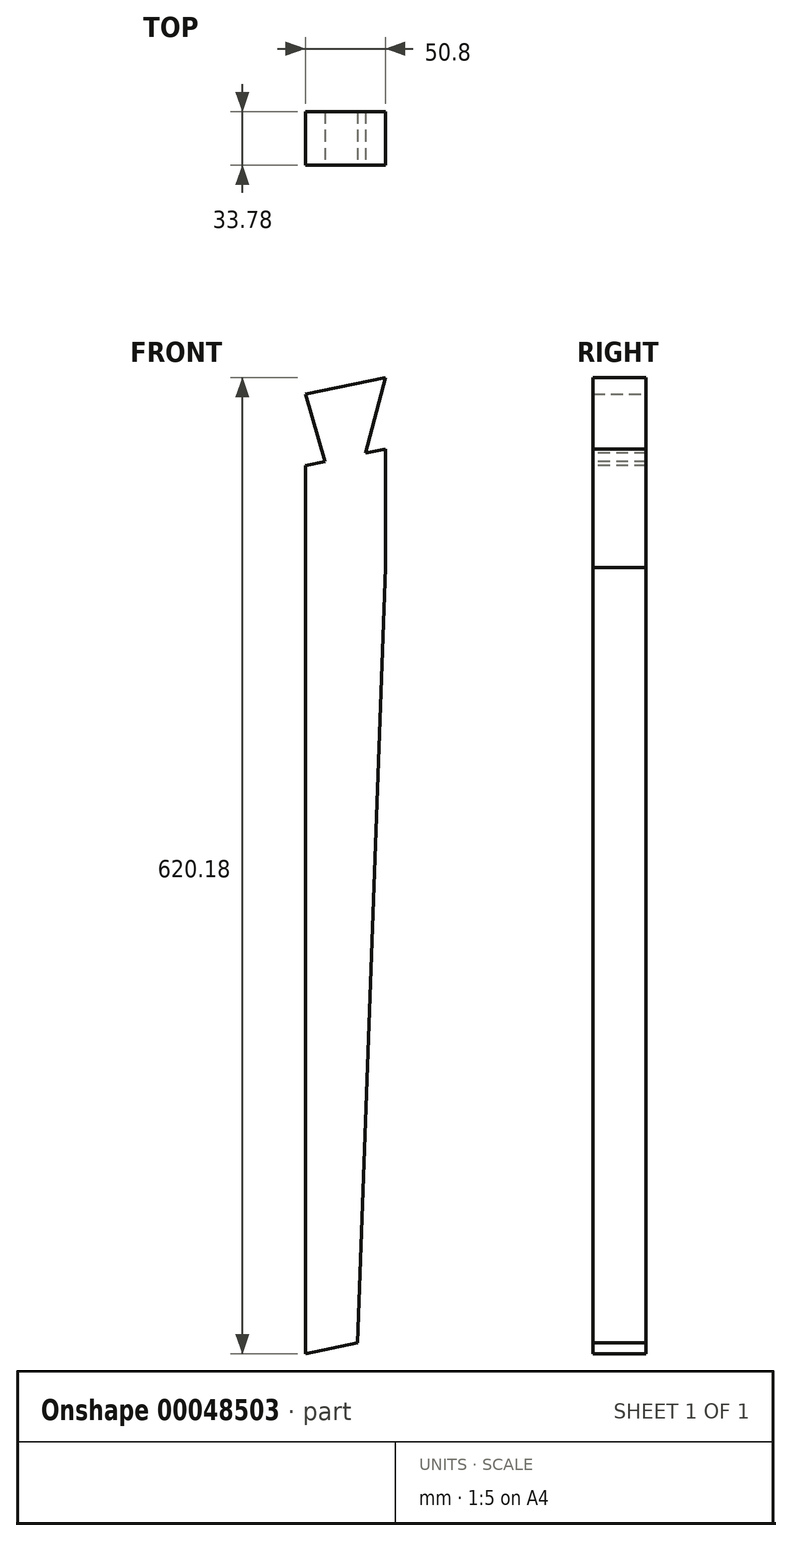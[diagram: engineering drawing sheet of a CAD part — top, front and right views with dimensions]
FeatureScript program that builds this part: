
annotation { "Feature Type Name" : "Feature", "Feature Type Description" : "" }
export const myFeature = defineFeature(function(context is Context, id is Id, definition is map)
    precondition{}
    {
        {
            var Q0;
            Q0=qCreatedBy(makeId("Front.planeOp"),FACE);
            var sketch = newSketch(context, id + "F0", { "sketchPlane" : qUnion([Q0])});
            skLineSegment(sketch, "E0.bottom", {"start": v(-25.4, 304.8) * mm, "end": v(25.4, 304.8) * mm});
            skLineSegment(sketch, "E0.top", {"start": v(-25.4, -315.38) * mm, "end": v(25.4, -315.38) * mm});
            skLineSegment(sketch, "E0.left", {"start": v(-25.4, 304.8) * mm, "end": v(-25.4, -315.38) * mm});
            skLineSegment(sketch, "E0.right", {"start": v(25.4, 304.8) * mm, "end": v(25.4, -315.38) * mm});
            skLineSegment(sketch, "E1", {"start": v(25.4, 304.8) * mm, "end": v(-584.2, 304.8) * mm, "construction": true});
            skLineSegment(sketch, "E2", {"start": v(-584.2, 304.8) * mm, "end": v(-584.2, 177.8) * mm, "construction": true});
            skLineSegment(sketch, "E3", {"start": v(-584.2, 177.8) * mm, "end": v(25.4, 304.8) * mm, "construction": true});
            skLineSegment(sketch, "E4", {"start": v(25.4, 304.8) * mm, "end": v(-25.4, 294.22) * mm});
            skLineSegment(sketch, "E5", {"start": v(-25.4, -315.38) * mm, "end": v(584.2, -315.38) * mm, "construction": true});
            skLineSegment(sketch, "E6", {"start": v(584.2, -315.38) * mm, "end": v(584.2, -188.38) * mm, "construction": true});
            skLineSegment(sketch, "E7", {"start": v(584.2, -188.38) * mm, "end": v(-25.4, -315.38) * mm, "construction": true});
            skLineSegment(sketch, "E8", {"start": v(-25.4, -315.38) * mm, "end": v(25.4, -304.8) * mm});
            skSolve(sketch);
        }
        {
            var Q0;
            {var subQ2=sQuery(id+"F0.wireOp",EDGE,"E4");Q0=makeQuery(id+"F0.imprint","IMPRINT",FACE,{"disambiguationData":[TD([[makeQuery(id+"F0.imprint","IMPRINT",EDGE,{"derivedFrom":subQ2}),1.0]])]});}
            extrude(context, id + "F1", {"entities" : qUnion([Q0]), "depth" : 33.78 * mm});
        }
        {
            var Q0;
            Q0=makeQuery(id+"F1.opExtrude","CAP_FACE",FACE,{"disambiguationData":[OSD([sQuery(id+"F0.wireOp",EDGE,"E0.left"),sQuery(id+"F0.wireOp",EDGE,"E0.right"),sQuery(id+"F0.wireOp",EDGE,"E4"),sQuery(id+"F0.wireOp",EDGE,"E8")])],"isStart":false});
            var sketch = newSketch(context, id + "F2", { "sketchPlane" : qUnion([Q0])});
            skLineSegment(sketch, "E9", {"start": v(-25.4, -315.38) * mm, "end": v(7.67, -308.5) * mm});
            skLineSegment(sketch, "E10", {"start": v(7.67, -308.5) * mm, "end": v(25.4, 184.15) * mm});
            skSolve(sketch);
        }
        {
            var Q0;
            {var subQ0=sQuery(id+"F2.wireOp",EDGE,"E10");Q0=makeQuery(id+"F2.imprint","IMPRINT",FACE,{"disambiguationData":[TD([[makeQuery(id+"F2.imprint","IMPRINT",EDGE,{"derivedFrom":subQ0}),-1.0]])]});}
            extrude(context, id + "F3", {"entities" : qUnion([Q0]), "operationType" : NewBodyOperationType.REMOVE, "endBound" : BoundingType.THROUGH_ALL, "oppositeDirection" : true, "depth" : 25.4 * mm});
        }
        {
            var Q0;
            Q0=makeQuery(id+"F1.opExtrude","CAP_FACE",FACE,{"disambiguationData":[OSD([sQuery(id+"F0.wireOp",EDGE,"E0.left"),sQuery(id+"F0.wireOp",EDGE,"E0.right"),sQuery(id+"F0.wireOp",EDGE,"E4"),sQuery(id+"F0.wireOp",EDGE,"E8")])],"isStart":false});
            var sketch = newSketch(context, id + "F4", { "sketchPlane" : qUnion([Q0])});
            skLineSegment(sketch, "E11", {"start": v(-25.4, 248.81) * mm, "end": v(25.4, 259.4) * mm, "construction": true});
            skLineSegment(sketch, "E12", {"start": v(-25.4, 248.81) * mm, "end": v(-12.97, 251.4) * mm});
            skLineSegment(sketch, "E13", {"start": v(25.4, 259.4) * mm, "end": v(12.97, 256.8) * mm});
            skLineSegment(sketch, "E14.0", {"start": v(25.4, 304.8) * mm, "end": v(-25.4, 294.22) * mm});
            skLineSegment(sketch, "E15", {"start": v(12.97, 256.8) * mm, "end": v(25.4, 304.8) * mm});
            skLineSegment(sketch, "E16", {"start": v(-12.97, 251.4) * mm, "end": v(-25.4, 294.22) * mm});
            skSolve(sketch);
        }
        {
            var Q0;
            {var subQ0=sQuery(id+"F4.wireOp",EDGE,"E12");Q0=makeQuery(id+"F4.imprint","IMPRINT",FACE,{"disambiguationData":[TD([[makeQuery(id+"F4.imprint","IMPRINT",EDGE,{"derivedFrom":subQ0}),1.0]])]});}
            var Q1;
            {var subQ0=sQuery(id+"F4.wireOp",EDGE,"E13");Q1=makeQuery(id+"F4.imprint","IMPRINT",FACE,{"disambiguationData":[TD([[makeQuery(id+"F4.imprint","IMPRINT",EDGE,{"derivedFrom":subQ0}),-1.0]])]});}
            extrude(context, id + "F5", {"entities" : qUnion([Q0, Q1]), "operationType" : NewBodyOperationType.REMOVE, "endBound" : BoundingType.THROUGH_ALL, "oppositeDirection" : true, "depth" : 25.4 * mm});
        }
    });
